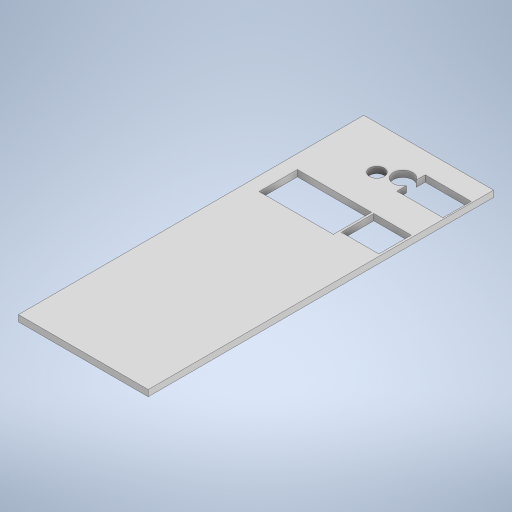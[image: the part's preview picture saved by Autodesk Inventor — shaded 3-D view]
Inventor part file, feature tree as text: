
AUTODESK INVENTOR PART (.ipt)
format: ipt  version: 2023 (Build 270158000, 158)  size: 292,352 bytes
history: native  units: in
note: dims shown in document units (in); Inventor stores cm internally (conversion verified against a paired STEP export)
features: extrude x2, sketch x2
ambient origin geometry x8: Origin, YZ Plane, XZ Plane, XY Plane, X Axis, Y Axis, Z Axis, Center Point
bodies: Solid1 (feature_tree)
feature tree (4):
  extrude  "Extrusion1"  Depth=2.4409in
  extrude  "Extrusion2"  Depth=6.4961in
  sketch  "Sketch1"  dims[d0=6.4961in d1=2.4409in]
  sketch  "Sketch2"  dims[d2=0.1181in d3=0.0in d4=0.0394in d5=0.0394in d6=0.0394in d7=0.0394in d8=0.0394in d9=0.0394in d10=0.0394in d11=0.0394in d12=0.0591in d13=0.0394in d14=0.0197in d15=0.0787in d16=0.0394in d17=0.0394in d18=0.3642in d19=0.2756in d20=1.5472in d21=2.1181in d22=0.3937in d23=0.9252in d24=1.5492in d25=2.189in d26=1.5492in d27=2.189in d28=0.0144in d29=0.6797in d30=0.7605in d31=0.8268in d32=2.1148in d33=2.4154in d36=0.1437in d37=1.5591in d38=2.0669in d39=0.0655in d40=0.0911in d41=0.2817in d42=0.6679in d43=1.5591in d44=2.0669in d45=1.6496in d46=2.0886in d47=0.9002in d48=0.9002in d49=1.0236in d50=1.0931in d51=1.29in d52=0.7087in d53=1.3622in d54=1.3622in d55=1.6246in d56=1.8215in d57=2.0144in d58=2.0144in d59=1.6496in d60=2.0886in d61=0.0in d62=6.4961in d63=4.9744in d64=0.0in d65=0.0in]
